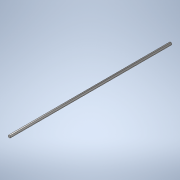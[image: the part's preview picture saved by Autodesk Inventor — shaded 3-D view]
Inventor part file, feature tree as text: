
AUTODESK INVENTOR PART (.ipt)
format: ipt  version: 2020 (Build 240168000, 168)  size: 110,080 bytes
history: native  units: in
note: dims shown in document units (in); Inventor stores cm internally (conversion verified against a paired STEP export)
features: extrude x1, sketch x1
ambient origin geometry x8: Origin, YZ Plane, XZ Plane, XY Plane, X Axis, Y Axis, Z Axis, Center Point
bodies: Solid1 (feature_tree)
feature tree (2):
  extrude  "Extrusion1"  Depth=36.0in TaperAngle=0.0deg
  sketch  "Sketch1"  dims[d0=0.5in d1=36.0in d2=0.0in]
